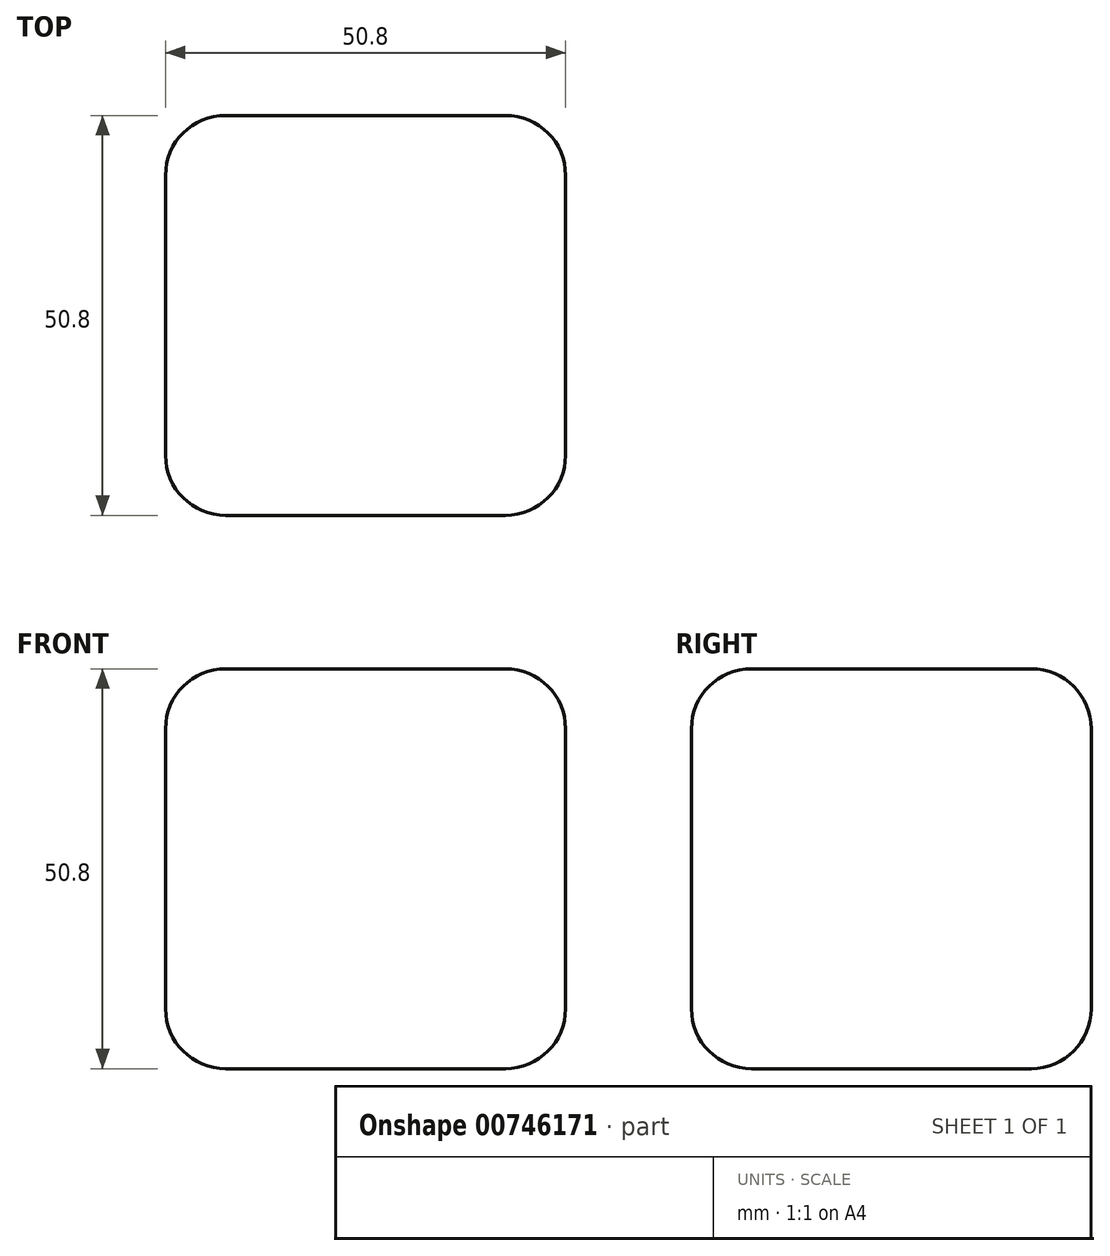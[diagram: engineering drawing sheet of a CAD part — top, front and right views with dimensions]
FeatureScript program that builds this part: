
annotation { "Feature Type Name" : "Feature", "Feature Type Description" : "" }
export const myFeature = defineFeature(function(context is Context, id is Id, definition is map)
    precondition{}
    {
        {
            var Q0;
            Q0=qCreatedBy(makeId("Top.planeOp"),FACE);
            var sketch = newSketch(context, id + "F0", { "sketchPlane" : qUnion([Q0])});
            skLineSegment(sketch, "E0.bottom", {"start": v(-24.79, 24.3) * mm, "end": v(26.01, 24.3) * mm});
            skLineSegment(sketch, "E0.top", {"start": v(-24.79, -26.5) * mm, "end": v(26.01, -26.5) * mm});
            skLineSegment(sketch, "E0.left", {"start": v(-24.79, 24.3) * mm, "end": v(-24.79, -26.5) * mm});
            skLineSegment(sketch, "E0.right", {"start": v(26.01, 24.3) * mm, "end": v(26.01, -26.5) * mm});
            skSolve(sketch);
        }
        {
            var Q0;
            Q0=makeQuery(id+"F0.imprint","IMPRINT",FACE,{"disambiguationData":[TD([[makeQuery(id+"F0.imprint","IMPRINT",EDGE,{"derivedFrom":sQuery(id+"F0.wireOp",EDGE,"E0.bottom")}),-1.0]])]});
            extrude(context, id + "F1", {"entities" : qUnion([Q0]), "depth" : 50.8 * mm, "offsetDistance" : 25.4 * mm});
        }
        {
            var Q0;
            Q0=makeQuery(id+"F1.opExtrude","SWEPT_FACE",FACE,{"disambiguationData":[OSD([sQuery(id+"F0.wireOp",EDGE,"E0.right")])]});
            var Q1;
            Q1=makeQuery(id+"F1.opExtrude","SWEPT_FACE",FACE,{"disambiguationData":[OSD([sQuery(id+"F0.wireOp",EDGE,"E0.bottom")])]});
            var Q2;
            Q2=makeQuery(id+"F1.opExtrude","CAP_FACE",FACE,{"disambiguationData":[OSD([sQuery(id+"F0.wireOp",EDGE,"E0.bottom"),sQuery(id+"F0.wireOp",EDGE,"E0.top"),sQuery(id+"F0.wireOp",EDGE,"E0.left"),sQuery(id+"F0.wireOp",EDGE,"E0.right")])],"isStart":false});
            var Q3;
            Q3=makeQuery(id+"F1.opExtrude","SWEPT_FACE",FACE,{"disambiguationData":[OSD([sQuery(id+"F0.wireOp",EDGE,"E0.top")])]});
            var Q4;
            Q4=makeQuery(id+"F1.opExtrude","SWEPT_FACE",FACE,{"disambiguationData":[OSD([sQuery(id+"F0.wireOp",EDGE,"E0.left")])]});
            fillet(context, id + "F2", {"entities" : qUnion([Q0, Q1, Q2, Q3, Q4]), "radius" : 7.62 * mm, "tangentPropagation" : true, "allowEdgeOverflow" : false});
        }
    });
